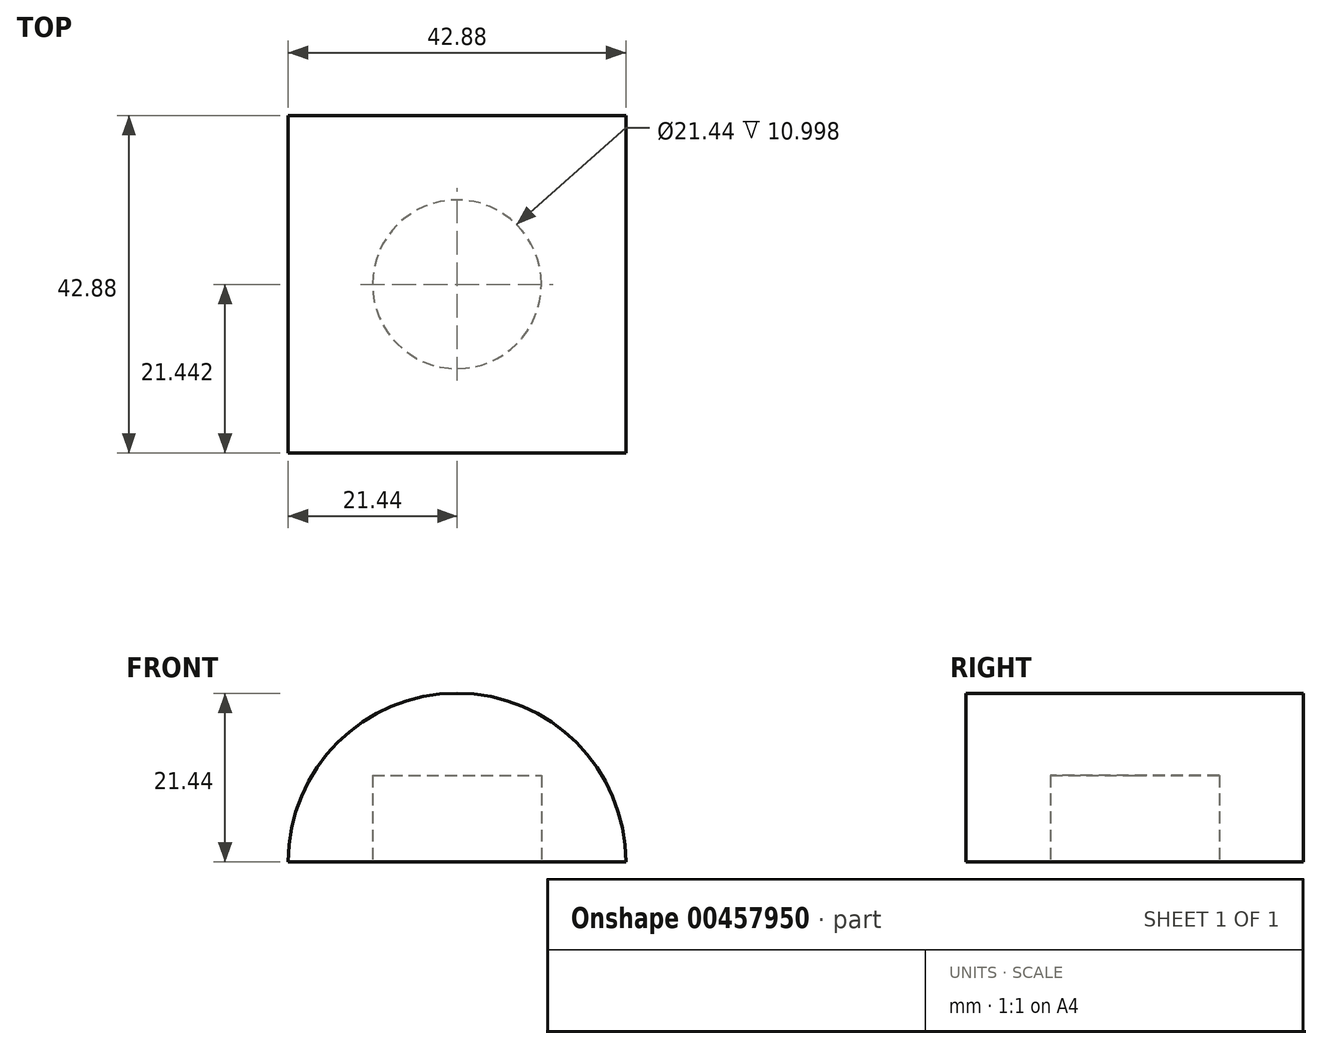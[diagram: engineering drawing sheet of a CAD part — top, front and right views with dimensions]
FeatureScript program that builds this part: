
annotation { "Feature Type Name" : "Feature", "Feature Type Description" : "" }
export const myFeature = defineFeature(function(context is Context, id is Id, definition is map)
    precondition{}
    {
        {
            var Q0;
            Q0=qCreatedBy(makeId("Front.planeOp"),FACE);
            var sketch = newSketch(context, id + "F0", { "sketchPlane" : qUnion([Q0])});
            skArc(sketch, "E0", {"start": v(21.44, 0) * mm, "mid": v(0, 21.44) * mm, "end": v(-21.44, 0) * mm});
            skLineSegment(sketch, "E1", {"start": v(-21.44, 0) * mm, "end": v(21.44, 0) * mm});
            skSolve(sketch);
        }
        {
            var Q0;
            Q0=qSketchRegion(id+"F0",true);
            extrude(context, id + "F1", {"entities" : qUnion([Q0]), "depth" : 42.88 * mm, "offsetDistance" : 25.4 * mm});
        }
        {
            var Q0;
            Q0=makeQuery(id+"F1.opExtrude","SWEPT_FACE",FACE,{"disambiguationData":[OSD([sQuery(id+"F0.wireOp",EDGE,"E1")])]});
            var sketch = newSketch(context, id + "F2", { "sketchPlane" : qUnion([Q0])});
            skCircle(sketch, "E2", {"center": v(0, 21.44) * mm, "radius": 10.72 * mm});
            skSolve(sketch);
        }
        {
            var Q0;
            Q0=qSketchRegion(id+"F2",true);
            extrude(context, id + "F3", {"entities" : qUnion([Q0]), "operationType" : NewBodyOperationType.REMOVE, "oppositeDirection" : true, "depth" : 11 * mm, "offsetDistance" : 25.4 * mm});
        }
    });
